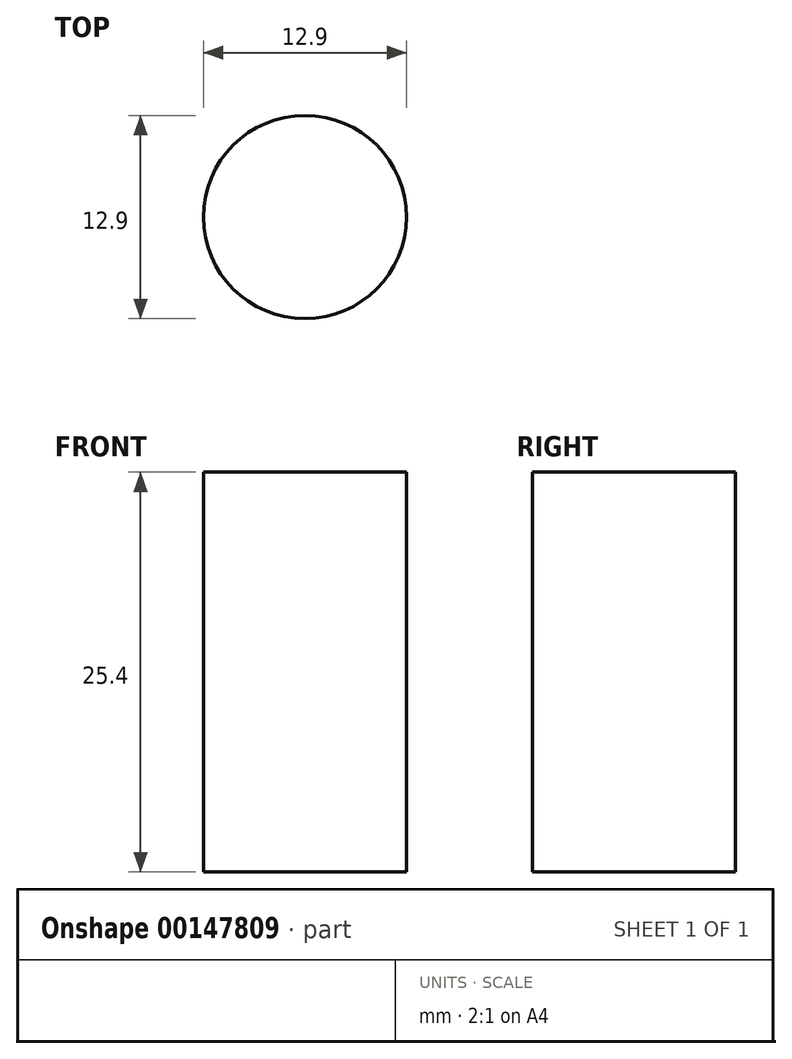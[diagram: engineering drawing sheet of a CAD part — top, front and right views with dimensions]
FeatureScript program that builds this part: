
annotation { "Feature Type Name" : "Feature", "Feature Type Description" : "" }
export const myFeature = defineFeature(function(context is Context, id is Id, definition is map)
    precondition{}
    {
        {
            var Q0;
            Q0=qCreatedBy(makeId("Top.planeOp"),FACE);
            var sketch = newSketch(context, id + "F0", { "sketchPlane" : qUnion([Q0])});
            skCircle(sketch, "E0", {"center": v(0, 0) * mm, "radius": 23.02 * mm});
            skLineSegment(sketch, "E1", {"start": v(0, 0) * mm, "end": v(75.86, 0) * mm, "construction": true});
            skLineSegment(sketch, "E2", {"start": v(75.86, 18.95) * mm, "end": v(75.86, -18.95) * mm, "construction": true});
            skLineSegment(sketch, "E3", {"start": v(75.86, 18.95) * mm, "end": v(75.86, 26.32) * mm, "construction": true});
            skLineSegment(sketch, "E4", {"start": v(75.86, -18.95) * mm, "end": v(75.86, -26.32) * mm, "construction": true});
            skCircle(sketch, "E5", {"center": v(75.86, 18.95) * mm, "radius": 18.16 * mm});
            skCircle(sketch, "E6", {"center": v(75.86, -18.95) * mm, "radius": 18.16 * mm});
            skCircle(sketch, "E7", {"center": v(75.86, 26.32) * mm, "radius": 6.45 * mm});
            skLineSegment(sketch, "E8", {"start": v(-2.9, 22.84) * mm, "end": v(75.05, 32.72) * mm});
            skLineSegment(sketch, "E9", {"start": v(76.67, 19.92) * mm, "end": v(47.9, 16.27) * mm});
            skArc(sketch, "E10", {"start": v(47.9, 16.27) * mm, "mid": v(43, 14.67) * mm, "end": v(39.04, 11.37) * mm});
            skLineSegment(sketch, "E11", {"start": v(39.04, 11.37) * mm, "end": v(17.82, -14.58) * mm});
            skCircle(sketch, "E12", {"center": v(49.6, 2.73) * mm, "radius": 12.7 * mm, "construction": true});
            skLineSegment(sketch, "E13", {"start": v(0, 0) * mm, "end": v(17.82, -14.58) * mm});
            skSolve(sketch);
        }
        {
            var Q0;
            {var subQ0=sQuery(id+"F0.wireOp",EDGE,"E7");var subQ1=makeQuery(id+"F0.imprint","INTERSECT",VERTEX,{"derivedFrom":[subQ0,sQuery(id+"F0.wireOp",EDGE,"E8")]});Q0=makeQuery(id+"F0.imprint","IMPRINT",FACE,{"disambiguationData":[TD([[makeQuery(id+"F0.imprint","IMPRINT",EDGE,{"disambiguationData":[TD([[subQ1,-1.0]])],"derivedFrom":subQ0}),1.0]])]});}
            extrude(context, id + "F1", {"entities" : qUnion([Q0]), "depth" : 25.4 * mm});
        }
    });
